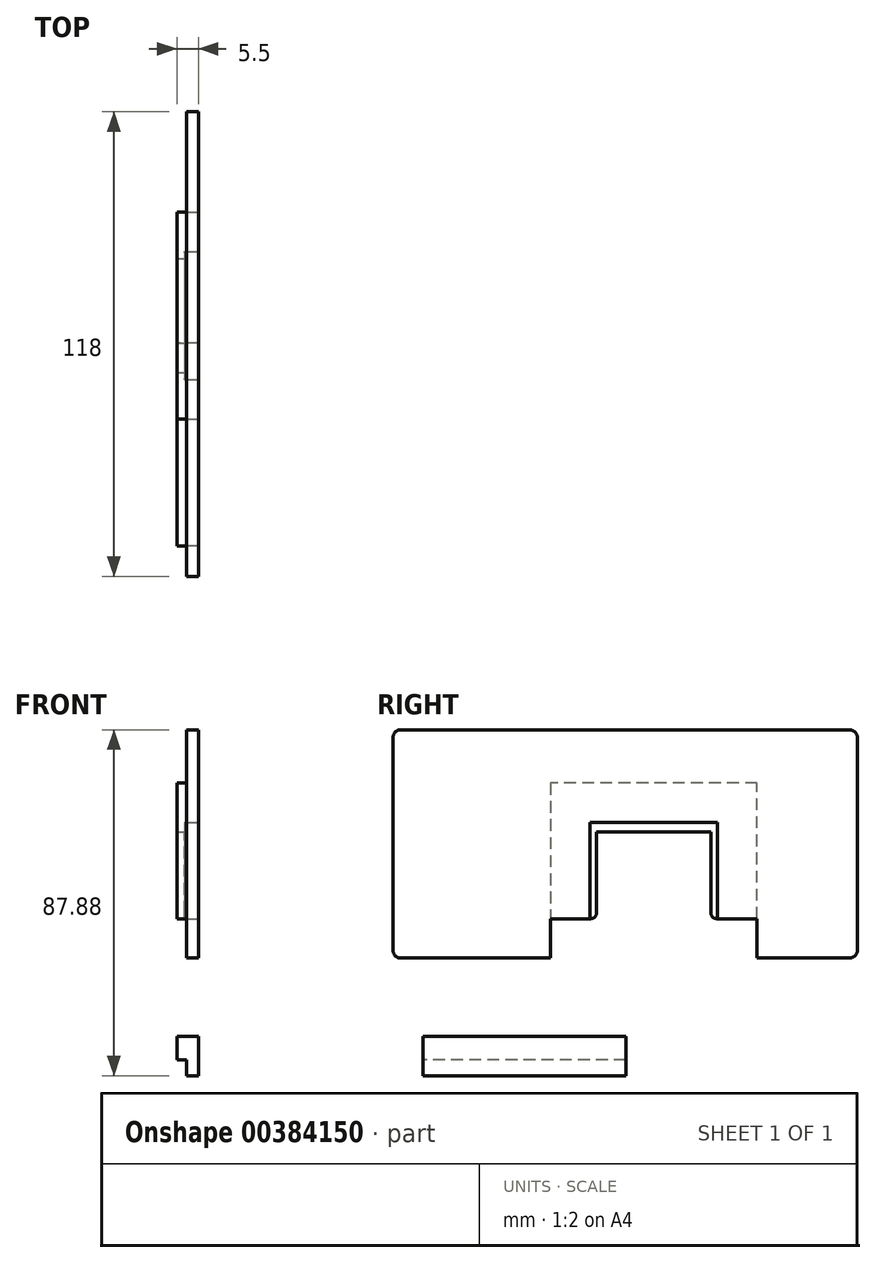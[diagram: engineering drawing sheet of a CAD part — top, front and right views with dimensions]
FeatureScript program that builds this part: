
annotation { "Feature Type Name" : "Feature", "Feature Type Description" : "" }
export const myFeature = defineFeature(function(context is Context, id is Id, definition is map)
    precondition{}
    {
        {
            var Q0;
            Q0=qCreatedBy(makeId("Right.planeOp"),FACE);
            var sketch = newSketch(context, id + "F0", { "sketchPlane" : qUnion([Q0])});
            skLineSegment(sketch, "E0.bottom", {"start": v(-57.2, 28.98) * mm, "end": v(56.8, 28.98) * mm});
            skLineSegment(sketch, "E0.top", {"start": v(-57.2, -29.02) * mm, "end": v(56.8, -29.02) * mm});
            skLineSegment(sketch, "E0.left", {"start": v(-59.2, 26.98) * mm, "end": v(-59.2, -27.02) * mm});
            skLineSegment(sketch, "E0.right", {"start": v(58.8, 26.98) * mm, "end": v(58.8, -27.02) * mm});
            skPoint(sketch, "E1.visualSharp", {"position": v(58.8, -29.02) * mm});
            skArc(sketch, "E1.filletArc", {"start": v(56.8, -29.02) * mm, "mid": v(58.22, -28.43) * mm, "end": v(58.8, -27.02) * mm});
            skPoint(sketch, "E2.visualSharp", {"position": v(58.8, 28.98) * mm});
            skArc(sketch, "E2.filletArc", {"start": v(58.8, 26.98) * mm, "mid": v(58.22, 28.4) * mm, "end": v(56.8, 28.98) * mm});
            skPoint(sketch, "E3.visualSharp", {"position": v(-59.2, -29.02) * mm});
            skArc(sketch, "E3.filletArc", {"start": v(-59.2, -27.02) * mm, "mid": v(-58.61, -28.43) * mm, "end": v(-57.2, -29.02) * mm});
            skPoint(sketch, "E4.visualSharp", {"position": v(-59.2, 28.98) * mm});
            skArc(sketch, "E4.filletArc", {"start": v(-57.2, 28.98) * mm, "mid": v(-58.61, 28.4) * mm, "end": v(-59.2, 26.98) * mm});
            skLineSegment(sketch, "E5.bottom", {"start": v(-51.5, -48.9) * mm, "end": v(0, -48.9) * mm});
            skLineSegment(sketch, "E5.top", {"start": v(-51.5, -58.9) * mm, "end": v(0, -58.9) * mm});
            skLineSegment(sketch, "E5.left", {"start": v(-51.5, -48.9) * mm, "end": v(-51.5, -58.9) * mm});
            skLineSegment(sketch, "E5.right", {"start": v(0, -48.9) * mm, "end": v(0, -58.9) * mm});
            skSolve(sketch);
        }
        {
            var Q0;
            Q0=makeQuery(id+"F0.imprint","IMPRINT",FACE,{"disambiguationData":[TD([[makeQuery(id+"F0.imprint","IMPRINT",EDGE,{"derivedFrom":sQuery(id+"F0.wireOp",EDGE,"E0.bottom")}),-1.0]])]});
            var Q1;
            Q1=makeQuery(id+"F0.imprint","IMPRINT",FACE,{"disambiguationData":[TD([[makeQuery(id+"F0.imprint","IMPRINT",EDGE,{"derivedFrom":sQuery(id+"F0.wireOp",EDGE,"E5.bottom")}),-1.0]])]});
            extrude(context, id + "F1", {"entities" : qUnion([Q0, Q1]), "depth" : 3 * mm});
        }
        {
            var Q0;
            Q0=makeQuery(id+"F1.opExtrude","CAP_FACE",FACE,{"disambiguationData":[OSD([sQuery(id+"F0.wireOp",EDGE,"E0.bottom"),sQuery(id+"F0.wireOp",EDGE,"E0.top"),sQuery(id+"F0.wireOp",EDGE,"E0.left"),sQuery(id+"F0.wireOp",EDGE,"E0.right"),sQuery(id+"F0.wireOp",EDGE,"E1.filletArc"),sQuery(id+"F0.wireOp",EDGE,"E2.filletArc"),sQuery(id+"F0.wireOp",EDGE,"E3.filletArc"),sQuery(id+"F0.wireOp",EDGE,"E4.filletArc")])],"isStart":false});
            var sketch = newSketch(context, id + "F2", { "sketchPlane" : qUnion([Q0])});
            skLineSegment(sketch, "E6.bottom", {"start": v(23.3, 5.48) * mm, "end": v(-9.2, 5.48) * mm});
            skLineSegment(sketch, "E6.top", {"start": v(23.3, -19.02) * mm, "end": v(-9.2, -19.02) * mm});
            skLineSegment(sketch, "E6.left", {"start": v(23.3, 5.48) * mm, "end": v(23.3, -19.02) * mm});
            skLineSegment(sketch, "E6.right", {"start": v(-9.2, 5.48) * mm, "end": v(-9.2, -19.02) * mm});
            skPoint(sketch, "E6.middle", {"position": v(7.05, -6.77) * mm});
            skLineSegment(sketch, "E7.bottom", {"start": v(-19.2, -19.02) * mm, "end": v(33.3, -19.02) * mm});
            skLineSegment(sketch, "E7.top", {"start": v(-19.2, -29.02) * mm, "end": v(33.3, -29.02) * mm});
            skLineSegment(sketch, "E7.left", {"start": v(-19.2, -19.02) * mm, "end": v(-19.2, -29.02) * mm});
            skLineSegment(sketch, "E7.right", {"start": v(33.3, -19.02) * mm, "end": v(33.3, -29.02) * mm});
            skSolve(sketch);
        }
        {
            var Q0;
            Q0=makeQuery(id+"F2.imprint","IMPRINT",FACE,{"disambiguationData":[TD([[makeQuery(id+"F2.imprint","IMPRINT",EDGE,{"derivedFrom":sQuery(id+"F2.wireOp",EDGE,"E6.bottom")}),1.0]])]});
            var Q1;
            Q1=makeQuery(id+"F2.imprint","IMPRINT",FACE,{"disambiguationData":[TD([[makeQuery(id+"F2.imprint","IMPRINT",EDGE,{"derivedFrom":sQuery(id+"F2.wireOp",EDGE,"E7.top")}),1.0]])]});
            extrude(context, id + "F3", {"entities" : qUnion([Q0, Q1]), "operationType" : NewBodyOperationType.REMOVE, "oppositeDirection" : true, "depth" : 3.5 * mm});
        }
        {
            var Q0;
            Q0=makeQuery(id+"F1.opExtrude","CAP_FACE",FACE,{"disambiguationData":[OSD([sQuery(id+"F0.wireOp",EDGE,"E0.bottom"),sQuery(id+"F0.wireOp",EDGE,"E0.top"),sQuery(id+"F0.wireOp",EDGE,"E0.left"),sQuery(id+"F0.wireOp",EDGE,"E0.right"),sQuery(id+"F0.wireOp",EDGE,"E1.filletArc"),sQuery(id+"F0.wireOp",EDGE,"E2.filletArc"),sQuery(id+"F0.wireOp",EDGE,"E3.filletArc"),sQuery(id+"F0.wireOp",EDGE,"E4.filletArc")])],"isStart":true});
            var sketch = newSketch(context, id + "F4", { "sketchPlane" : qUnion([Q0])});
            skLineSegment(sketch, "E8", {"start": v(-33.3, -19.02) * mm, "end": v(-33.3, 15.48) * mm});
            skLineSegment(sketch, "E9", {"start": v(-33.3, 15.48) * mm, "end": v(19.2, 15.48) * mm});
            skLineSegment(sketch, "E10", {"start": v(19.2, 15.48) * mm, "end": v(19.2, -19.02) * mm});
            skLineSegment(sketch, "E11", {"start": v(-23.3, -19.02) * mm, "end": v(-21.55, -19.02) * mm});
            skLineSegment(sketch, "E12", {"start": v(-21.55, -19.02) * mm, "end": v(-21.55, 2.98) * mm});
            skLineSegment(sketch, "E13", {"start": v(-21.55, 2.98) * mm, "end": v(7.45, 2.98) * mm});
            skLineSegment(sketch, "E14", {"start": v(7.45, 2.98) * mm, "end": v(7.45, -19.02) * mm});
            skLineSegment(sketch, "E15", {"start": v(7.45, -19.02) * mm, "end": v(9.2, -19.02) * mm});
            skSolve(sketch);
        }
        {
            var Q0;
            Q0=makeQuery(id+"F4.imprint","IMPRINT",FACE,{"disambiguationData":[TD([[makeQuery(id+"F4.imprint","IMPRINT",EDGE,{"derivedFrom":sQuery(id+"F4.wireOp",EDGE,"E8")}),-1.0]])]});
            var Q1;
            Q1=makeQuery(id+"F4.imprint","IMPRINT",FACE,{"disambiguationData":[TD([[makeQuery(id+"F4.imprint","IMPRINT",EDGE,{"derivedFrom":sQuery(id+"F4.wireOp",EDGE,"E11")}),1.0]])]});
            extrude(context, id + "F5", {"entities" : qUnion([Q0, Q1]), "operationType" : NewBodyOperationType.ADD, "depth" : 2.5 * mm});
        }
        {
            var Q0;
            Q0=makeQuery(id+"F5.opExtrude","CAP_FACE",FACE,{"disambiguationData":[OSD([sQuery(id+"F0.wireOp",EDGE,"E0.bottom"),sQuery(id+"F0.wireOp",EDGE,"E0.top"),sQuery(id+"F0.wireOp",EDGE,"E0.left"),sQuery(id+"F0.wireOp",EDGE,"E0.right"),sQuery(id+"F0.wireOp",EDGE,"E1.filletArc"),sQuery(id+"F0.wireOp",EDGE,"E2.filletArc"),sQuery(id+"F0.wireOp",EDGE,"E3.filletArc"),sQuery(id+"F0.wireOp",EDGE,"E4.filletArc"),sQuery(id+"F2.wireOp",EDGE,"E7.bottom"),sQuery(id+"F4.wireOp",EDGE,"E8"),sQuery(id+"F4.wireOp",EDGE,"E9"),sQuery(id+"F4.wireOp",EDGE,"E10"),sQuery(id+"F4.wireOp",EDGE,"E11"),sQuery(id+"F4.wireOp",EDGE,"E12"),sQuery(id+"F4.wireOp",EDGE,"E13"),sQuery(id+"F4.wireOp",EDGE,"E14"),sQuery(id+"F4.wireOp",EDGE,"E15")])],"isStart":true});
            extrude(context, id + "F6", {"entities" : qUnion([Q0]), "operationType" : NewBodyOperationType.REMOVE, "oppositeDirection" : true, "depth" : .5 * mm});
        }
        {
            var Q0;
            Q0=makeQuery(id+"F1.opExtrude","CAP_FACE",FACE,{"disambiguationData":[OSD([sQuery(id+"F0.wireOp",EDGE,"E5.bottom"),sQuery(id+"F0.wireOp",EDGE,"E5.top"),sQuery(id+"F0.wireOp",EDGE,"E5.left"),sQuery(id+"F0.wireOp",EDGE,"E5.right")])],"isStart":true});
            var sketch = newSketch(context, id + "F7", { "sketchPlane" : qUnion([Q0])});
            skLineSegment(sketch, "E16", {"start": v(0, -54.9) * mm, "end": v(51.5, -54.9) * mm});
            skSolve(sketch);
        }
        {
            var Q0;
            {var subQ0=sQuery(id+"F7.wireOp",EDGE,"E16");Q0=makeQuery(id+"F7.imprint","IMPRINT",FACE,{"disambiguationData":[TD([[makeQuery(id+"F7.imprint","IMPRINT",EDGE,{"derivedFrom":subQ0}),1.0]])]});}
            extrude(context, id + "F8", {"entities" : qUnion([Q0]), "operationType" : NewBodyOperationType.ADD, "depth" : 2.5 * mm});
        }
        {
            var Q0;
            Q0=makeQuery(id+"F5.opExtrude","SWEPT_EDGE",EDGE,{"disambiguationData":[OSD([sQuery(id+"F4.wireOp",EDGE,"E14"),sQuery(id+"F4.wireOp",EDGE,"E15")])]});
            var Q1;
            Q1=makeQuery(id+"F5.opExtrude","SWEPT_EDGE",EDGE,{"disambiguationData":[OSD([sQuery(id+"F4.wireOp",EDGE,"E11"),sQuery(id+"F4.wireOp",EDGE,"E12")])]});
            fillet(context, id + "F9", {"entities" : qUnion([Q0, Q1]), "radius" : 1.5 * mm, "tangentPropagation" : true, "allowEdgeOverflow" : false});
        }
    });
